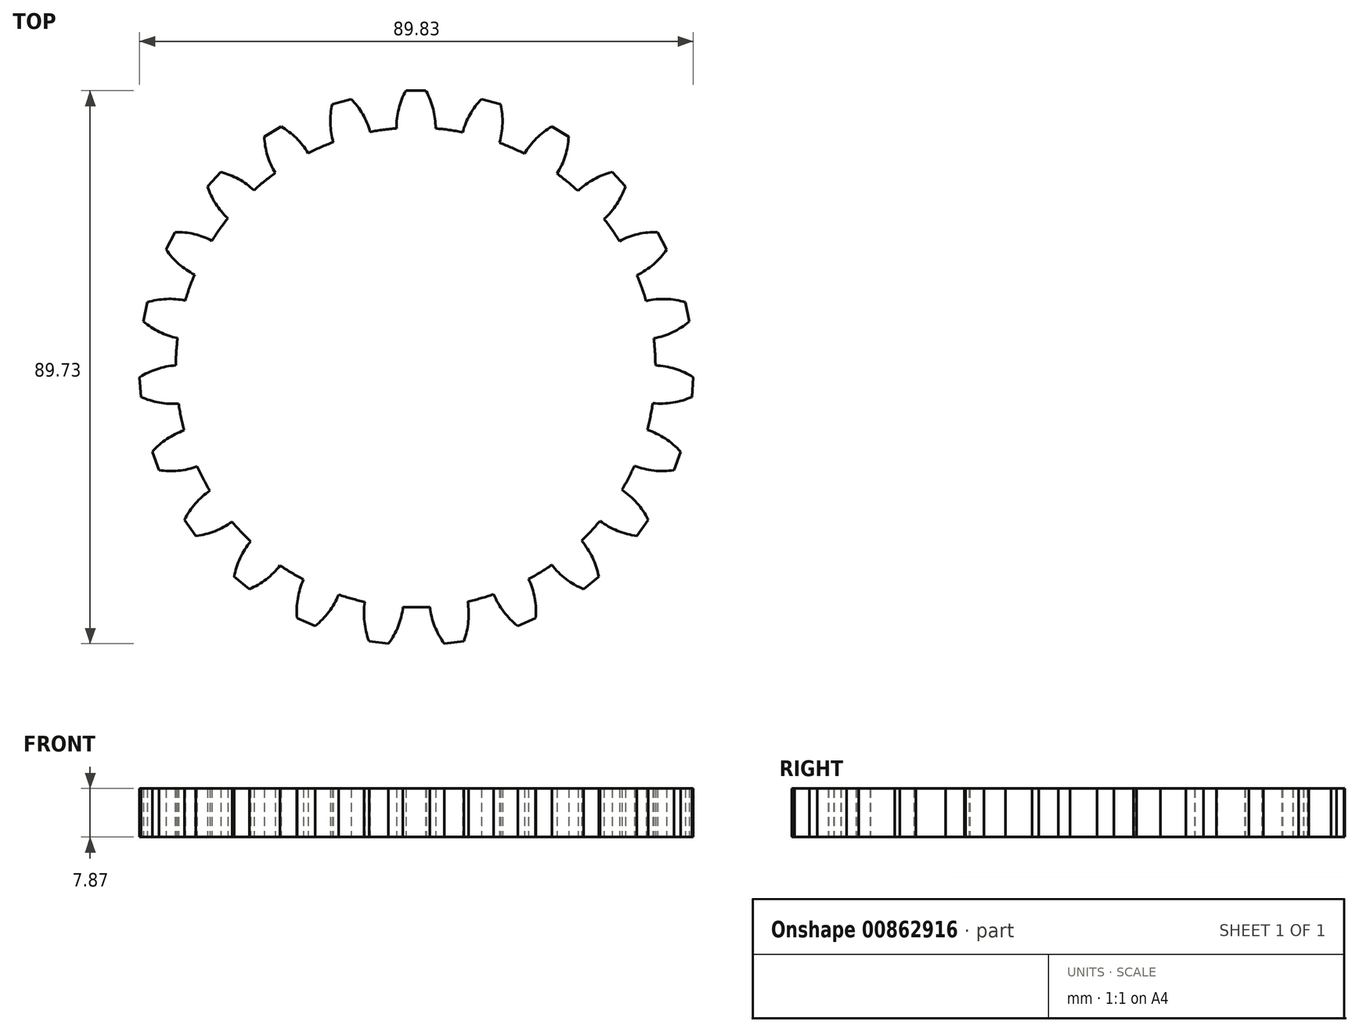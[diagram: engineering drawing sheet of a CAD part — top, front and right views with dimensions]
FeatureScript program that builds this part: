
annotation { "Feature Type Name" : "Feature", "Feature Type Description" : "" }
export const myFeature = defineFeature(function(context is Context, id is Id, definition is map)
    precondition{}
    {
        {
            var Q0;
            Q0=qCreatedBy(makeId("Top.planeOp"),FACE);
            var sketch = newSketch(context, id + "F0", { "sketchPlane" : qUnion([Q0])});
            skArc(sketch, "E0", {"start": v(-3.1, 38.8) * mm, "mid": v(0, -38.92) * mm, "end": v(3.1, 38.8) * mm});
            skArc(sketch, "E1", {"start": v(-1.6, 44.91) * mm, "mid": v(-2.74, 41.95) * mm, "end": v(-3.1, 38.8) * mm});
            skLineSegment(sketch, "E2", {"start": v(-1.6, 44.91) * mm, "end": v(0, 44.91) * mm});
            skArc(sketch, "E3.MirrorCS", {"start": v(1.6, 44.91) * mm, "mid": v(2.74, 41.95) * mm, "end": v(3.1, 38.8) * mm});
            skLineSegment(sketch, "E4.MirrorCS", {"start": v(1.6, 44.91) * mm, "end": v(0, 44.91) * mm});
            skLineSegment(sketch, "E5.anchor1", {"start": v(0, 0) * mm, "end": v(-9.25, 38.98) * mm, "construction": true});
            skLineSegment(sketch, "E5.anchor2", {"start": v(0, 0) * mm, "end": v(-9.25, 38.98) * mm, "construction": true});
            skArc(sketch, "E6", {"start": v(-1.46, 44.8) * mm, "mid": v(-2.62, 41.84) * mm, "end": v(-2.98, 38.68) * mm});
            skLineSegment(sketch, "E7", {"start": v(-1.46, 44.8) * mm, "end": v(0.13, 44.8) * mm});
            skArc(sketch, "E8.MirrorCS", {"start": v(1.72, 44.8) * mm, "mid": v(2.87, 41.84) * mm, "end": v(3.23, 38.68) * mm});
            skLineSegment(sketch, "E9.MirrorCS", {"start": v(1.72, 44.8) * mm, "end": v(0.13, 44.8) * mm});
            skArc(sketch, "E10.1.0", {"start": v(10.71, 43.56) * mm, "mid": v(8.8, 41.02) * mm, "end": v(7.6, 38.08) * mm});
            skArc(sketch, "E10.1.1", {"start": v(13.78, 42.7) * mm, "mid": v(14.09, 39.54) * mm, "end": v(13.58, 36.4) * mm});
            skLineSegment(sketch, "E10.1.2", {"start": v(10.71, 43.56) * mm, "end": v(12.24, 43.13) * mm});
            skLineSegment(sketch, "E10.1.3", {"start": v(13.78, 42.7) * mm, "end": v(12.24, 43.13) * mm});
            skArc(sketch, "E10.2.0", {"start": v(22.1, 39.09) * mm, "mid": v(19.58, 37.16) * mm, "end": v(17.63, 34.65) * mm});
            skArc(sketch, "E10.2.1", {"start": v(24.82, 37.43) * mm, "mid": v(24.27, 34.3) * mm, "end": v(22.94, 31.42) * mm});
            skLineSegment(sketch, "E10.2.2", {"start": v(22.1, 39.09) * mm, "end": v(23.46, 38.26) * mm});
            skLineSegment(sketch, "E10.2.3", {"start": v(24.82, 37.43) * mm, "end": v(23.46, 38.26) * mm});
            skArc(sketch, "E10.3.0", {"start": v(31.86, 31.7) * mm, "mid": v(28.9, 30.53) * mm, "end": v(26.35, 28.64) * mm});
            skArc(sketch, "E10.3.1", {"start": v(34.04, 29.38) * mm, "mid": v(32.65, 26.5) * mm, "end": v(30.57, 24.08) * mm});
            skLineSegment(sketch, "E10.3.2", {"start": v(31.86, 31.7) * mm, "end": v(32.95, 30.54) * mm});
            skLineSegment(sketch, "E10.3.3", {"start": v(34.04, 29.38) * mm, "end": v(32.95, 30.54) * mm});
            skArc(sketch, "E10.4.0", {"start": v(39.27, 21.96) * mm, "mid": v(36.08, 21.64) * mm, "end": v(33.08, 20.5) * mm});
            skArc(sketch, "E10.4.1", {"start": v(40.73, 19.14) * mm, "mid": v(38.58, 16.73) * mm, "end": v(35.87, 14.96) * mm});
            skLineSegment(sketch, "E10.4.2", {"start": v(39.27, 21.96) * mm, "end": v(40, 20.55) * mm});
            skLineSegment(sketch, "E10.4.3", {"start": v(40.73, 19.14) * mm, "end": v(40, 20.55) * mm});
            skArc(sketch, "E10.5.0", {"start": v(43.77, 10.58) * mm, "mid": v(40.6, 11.1) * mm, "end": v(37.4, 10.79) * mm});
            skArc(sketch, "E10.5.1", {"start": v(44.42, 7.47) * mm, "mid": v(41.7, 5.72) * mm, "end": v(38.63, 4.73) * mm});
            skLineSegment(sketch, "E10.5.2", {"start": v(43.77, 10.58) * mm, "end": v(44.1, 9.03) * mm});
            skLineSegment(sketch, "E10.5.3", {"start": v(44.42, 7.47) * mm, "end": v(44.1, 9.03) * mm});
            skArc(sketch, "E10.6.0", {"start": v(45.04, -1.59) * mm, "mid": v(42.1, -0.22) * mm, "end": v(38.92, 0.33) * mm});
            skArc(sketch, "E10.6.1", {"start": v(44.82, -4.77) * mm, "mid": v(41.72, -5.7) * mm, "end": v(38.48, -5.8) * mm});
            skLineSegment(sketch, "E10.6.2", {"start": v(45.04, -1.59) * mm, "end": v(44.93, -3.18) * mm});
            skLineSegment(sketch, "E10.6.3", {"start": v(44.82, -4.77) * mm, "end": v(44.93, -3.18) * mm});
            skArc(sketch, "E10.7.0", {"start": v(42.98, -13.65) * mm, "mid": v(40.5, -11.54) * mm, "end": v(37.58, -10.14) * mm});
            skArc(sketch, "E10.7.1", {"start": v(41.91, -16.65) * mm, "mid": v(38.66, -16.73) * mm, "end": v(35.5, -15.95) * mm});
            skLineSegment(sketch, "E10.7.2", {"start": v(42.98, -13.65) * mm, "end": v(42.44, -15.15) * mm});
            skLineSegment(sketch, "E10.7.3", {"start": v(41.91, -16.65) * mm, "end": v(42.44, -15.15) * mm});
            skArc(sketch, "E10.8.0", {"start": v(37.74, -24.71) * mm, "mid": v(35.92, -22) * mm, "end": v(33.47, -19.87) * mm});
            skArc(sketch, "E10.8.1", {"start": v(35.9, -27.31) * mm, "mid": v(32.75, -26.5) * mm, "end": v(29.91, -24.9) * mm});
            skLineSegment(sketch, "E10.8.2", {"start": v(37.74, -24.71) * mm, "end": v(36.82, -26.01) * mm});
            skLineSegment(sketch, "E10.8.3", {"start": v(35.9, -27.31) * mm, "end": v(36.82, -26.01) * mm});
            skArc(sketch, "E10.9.0", {"start": v(29.7, -33.95) * mm, "mid": v(28.7, -30.84) * mm, "end": v(26.91, -28.12) * mm});
            skArc(sketch, "E10.9.1", {"start": v(27.23, -35.95) * mm, "mid": v(24.4, -34.33) * mm, "end": v(22.1, -32.03) * mm});
            skLineSegment(sketch, "E10.9.2", {"start": v(29.7, -33.95) * mm, "end": v(28.47, -34.95) * mm});
            skLineSegment(sketch, "E10.9.3", {"start": v(27.23, -35.95) * mm, "end": v(28.47, -34.95) * mm});
            skArc(sketch, "E10.10.0", {"start": v(19.48, -40.67) * mm, "mid": v(19.33, -37.42) * mm, "end": v(18.34, -34.33) * mm});
            skArc(sketch, "E10.10.1", {"start": v(16.56, -41.94) * mm, "mid": v(14.28, -39.63) * mm, "end": v(12.68, -36.8) * mm});
            skLineSegment(sketch, "E10.10.2", {"start": v(19.48, -40.67) * mm, "end": v(18.02, -41.3) * mm});
            skLineSegment(sketch, "E10.10.3", {"start": v(16.56, -41.94) * mm, "end": v(18.02, -41.3) * mm});
            skArc(sketch, "E10.11.0", {"start": v(7.82, -44.39) * mm, "mid": v(8.56, -41.23) * mm, "end": v(8.45, -38) * mm});
            skArc(sketch, "E10.11.1", {"start": v(4.67, -44.82) * mm, "mid": v(3.1, -42) * mm, "end": v(2.3, -38.85) * mm});
            skLineSegment(sketch, "E10.11.2", {"start": v(7.82, -44.39) * mm, "end": v(6.24, -44.6) * mm});
            skLineSegment(sketch, "E10.11.3", {"start": v(4.67, -44.82) * mm, "end": v(6.24, -44.6) * mm});
            skArc(sketch, "E10.12.0", {"start": v(-4.41, -44.82) * mm, "mid": v(-2.84, -42) * mm, "end": v(-2.05, -38.87) * mm});
            skArc(sketch, "E10.12.1", {"start": v(-7.57, -44.39) * mm, "mid": v(-8.32, -41.26) * mm, "end": v(-8.23, -38.04) * mm});
            skLineSegment(sketch, "E10.12.2", {"start": v(-4.41, -44.82) * mm, "end": v(-5.99, -44.6) * mm});
            skLineSegment(sketch, "E10.12.3", {"start": v(-7.57, -44.39) * mm, "end": v(-5.99, -44.6) * mm});
            skArc(sketch, "E10.13.0", {"start": v(-16.3, -41.94) * mm, "mid": v(-14.07, -39.65) * mm, "end": v(-12.5, -36.86) * mm});
            skArc(sketch, "E10.13.1", {"start": v(-19.23, -40.67) * mm, "mid": v(-19.12, -37.47) * mm, "end": v(-18.2, -34.4) * mm});
            skLineSegment(sketch, "E10.13.2", {"start": v(-16.3, -41.94) * mm, "end": v(-17.77, -41.3) * mm});
            skLineSegment(sketch, "E10.13.3", {"start": v(-19.23, -40.67) * mm, "end": v(-17.77, -41.3) * mm});
            skArc(sketch, "E10.14.0", {"start": v(-26.98, -35.95) * mm, "mid": v(-24.2, -34.32) * mm, "end": v(-21.92, -32.02) * mm});
            skArc(sketch, "E10.14.1", {"start": v(-29.45, -33.95) * mm, "mid": v(-28.48, -30.92) * mm, "end": v(-26.76, -28.25) * mm});
            skLineSegment(sketch, "E10.14.2", {"start": v(-26.98, -35.95) * mm, "end": v(-28.22, -34.95) * mm});
            skLineSegment(sketch, "E10.14.3", {"start": v(-29.45, -33.95) * mm, "end": v(-28.22, -34.95) * mm});
            skArc(sketch, "E10.15.0", {"start": v(-35.65, -27.31) * mm, "mid": v(-32.56, -26.55) * mm, "end": v(-29.78, -25.02) * mm});
            skArc(sketch, "E10.15.1", {"start": v(-37.48, -24.71) * mm, "mid": v(-35.73, -22.06) * mm, "end": v(-33.36, -19.95) * mm});
            skLineSegment(sketch, "E10.15.2", {"start": v(-35.65, -27.31) * mm, "end": v(-36.56, -26.01) * mm});
            skLineSegment(sketch, "E10.15.3", {"start": v(-37.48, -24.71) * mm, "end": v(-36.56, -26.01) * mm});
            skArc(sketch, "E10.16.0", {"start": v(-41.66, -16.65) * mm, "mid": v(-38.48, -16.75) * mm, "end": v(-35.39, -16.03) * mm});
            skArc(sketch, "E10.16.1", {"start": v(-42.72, -13.65) * mm, "mid": v(-40.32, -11.57) * mm, "end": v(-37.47, -10.18) * mm});
            skLineSegment(sketch, "E10.16.2", {"start": v(-41.66, -16.65) * mm, "end": v(-42.2, -15.15) * mm});
            skLineSegment(sketch, "E10.16.3", {"start": v(-42.72, -13.65) * mm, "end": v(-42.2, -15.15) * mm});
            skArc(sketch, "E10.17.0", {"start": v(-44.57, -4.77) * mm, "mid": v(-41.54, -5.71) * mm, "end": v(-38.37, -5.86) * mm});
            skArc(sketch, "E10.17.1", {"start": v(-44.79, -1.59) * mm, "mid": v(-41.91, -0.24) * mm, "end": v(-38.79, 0.34) * mm});
            skLineSegment(sketch, "E10.17.2", {"start": v(-44.57, -4.77) * mm, "end": v(-44.68, -3.18) * mm});
            skLineSegment(sketch, "E10.17.3", {"start": v(-44.79, -1.59) * mm, "end": v(-44.68, -3.18) * mm});
            skArc(sketch, "E10.18.0", {"start": v(-44.17, 7.47) * mm, "mid": v(-41.5, 5.74) * mm, "end": v(-38.49, 4.74) * mm});
            skArc(sketch, "E10.18.1", {"start": v(-43.52, 10.58) * mm, "mid": v(-40.39, 11.11) * mm, "end": v(-37.23, 10.82) * mm});
            skLineSegment(sketch, "E10.18.2", {"start": v(-44.17, 7.47) * mm, "end": v(-43.84, 9.03) * mm});
            skLineSegment(sketch, "E10.18.3", {"start": v(-43.52, 10.58) * mm, "end": v(-43.84, 9.03) * mm});
            skArc(sketch, "E10.19.0", {"start": v(-40.48, 19.14) * mm, "mid": v(-38.38, 16.75) * mm, "end": v(-35.75, 14.98) * mm});
            skArc(sketch, "E10.19.1", {"start": v(-39.02, 21.96) * mm, "mid": v(-35.86, 21.62) * mm, "end": v(-32.9, 20.5) * mm});
            skLineSegment(sketch, "E10.19.2", {"start": v(-40.48, 19.14) * mm, "end": v(-39.75, 20.55) * mm});
            skLineSegment(sketch, "E10.19.3", {"start": v(-39.02, 21.96) * mm, "end": v(-39.75, 20.55) * mm});
            skArc(sketch, "E10.20.0", {"start": v(-33.78, 29.38) * mm, "mid": v(-32.4, 26.52) * mm, "end": v(-30.35, 24.1) * mm});
            skArc(sketch, "E10.20.1", {"start": v(-31.6, 31.7) * mm, "mid": v(-28.66, 30.53) * mm, "end": v(-26.1, 28.64) * mm});
            skLineSegment(sketch, "E10.20.2", {"start": v(-33.78, 29.38) * mm, "end": v(-32.7, 30.54) * mm});
            skLineSegment(sketch, "E10.20.3", {"start": v(-31.6, 31.7) * mm, "end": v(-32.7, 30.54) * mm});
            skArc(sketch, "E10.21.0", {"start": v(-24.57, 37.43) * mm, "mid": v(-24.02, 34.3) * mm, "end": v(-22.68, 31.42) * mm});
            skArc(sketch, "E10.21.1", {"start": v(-21.85, 39.09) * mm, "mid": v(-19.33, 37.16) * mm, "end": v(-17.38, 34.65) * mm});
            skLineSegment(sketch, "E10.21.2", {"start": v(-24.57, 37.43) * mm, "end": v(-23.2, 38.26) * mm});
            skLineSegment(sketch, "E10.21.3", {"start": v(-21.85, 39.09) * mm, "end": v(-23.2, 38.26) * mm});
            skArc(sketch, "E10.22.0", {"start": v(-13.52, 42.7) * mm, "mid": v(-13.83, 39.54) * mm, "end": v(-13.33, 36.4) * mm});
            skArc(sketch, "E10.22.1", {"start": v(-10.46, 43.56) * mm, "mid": v(-8.55, 41.02) * mm, "end": v(-7.35, 38.08) * mm});
            skLineSegment(sketch, "E10.22.2", {"start": v(-13.52, 42.7) * mm, "end": v(-12, 43.13) * mm});
            skLineSegment(sketch, "E10.22.3", {"start": v(-10.46, 43.56) * mm, "end": v(-12, 43.13) * mm});
            skSolve(sketch);
        }
        {
            var Q0;
            Q0 = qSketchRegion(id + "F0", true);
            extrude(context, id + "F1", {"entities" : qUnion([Q0]), "depth" : 7.87 * mm, "offsetDistance" : 25.4 * mm});
        }
    });
